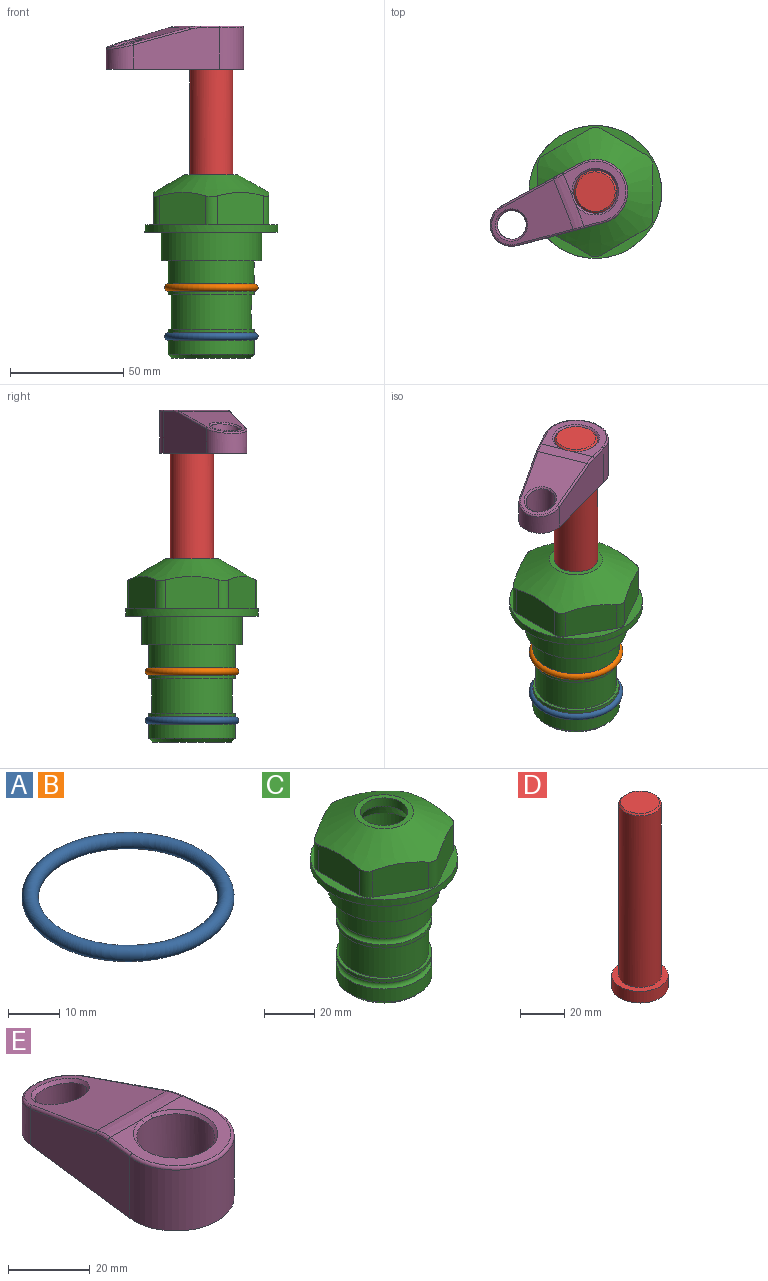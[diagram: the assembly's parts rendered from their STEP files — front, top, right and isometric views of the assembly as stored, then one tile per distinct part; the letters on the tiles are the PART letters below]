
ASSEMBLY  parts=5 mates=4
PART A: 1 faces, bbox 44.7x44.7x3.2 mm
  f0: torus R=19.05mm, axis (0,0,1), area 1193.9mm2
PART B: same geometry as A
PART C: 36 faces, bbox 58.7x58.7x81 mm
  f0: cylinder r=17.78mm len=35.56mm, axis (0,0,1), area 1670.8mm2, adj f23,f24,f31
  f1: cylinder r=19.05mm len=38.1mm, axis (0,0,1), area 1191.9mm2, adj f26,f27,f30
  f2: plane 58.66x58.66mm, normal (0,0,-1), area 1150.6mm2, adj f3,f28
  f3: cylinder r=29.33mm len=58.66mm, axis (0,0,-1), area 585.1mm2, adj f2,f4
  f4: plane 58.66x58.66mm, normal (0,0,1), area 475.9mm2, adj f3,f5,f6,f7,f8,f9,f10,f11
  f5: plane 20.32x14.34mm, normal (-0.5,0.87,0), area 324.4mm2, adj f4,f15,f16,f17
  f6: plane 20.32x14.34mm, normal (0.5,0.87,0), area 324.4mm2, adj f4,f14,f15,f17
  f7: plane 23.48x14.34mm, normal (1,0,0), area 324.4mm2, adj f4,f13,f14,f17
  f8: plane 20.32x14.34mm, normal (0.5,-0.87,0), area 324.4mm2, adj f4,f12,f13,f17
  f9: plane 20.32x14.34mm, normal (-0.5,-0.87,0), area 324.4mm2, adj f4,f11,f12,f17
  f10: plane 23.48x14.34mm, normal (-1,0,0), area 324.4mm2, adj f4,f11,f16,f17
  f11: cylinder r=5.08mm len=12.85mm, axis (0,0,-1), area 67.2mm2, adj f4,f9,f10,f17
  f12: cylinder r=5.08mm len=12.85mm, axis (0,0,-1), area 67.2mm2, adj f4,f8,f9,f17
  f13: cylinder r=5.08mm len=12.85mm, axis (0,0,-1), area 67.2mm2, adj f4,f7,f8,f17
  f14: cylinder r=5.08mm len=12.85mm, axis (0,0,-1), area 67.2mm2, adj f4,f6,f7,f17
  f15: cylinder r=5.08mm len=12.85mm, axis (0,0,-1), area 67.2mm2, adj f4,f5,f6,f17
  f16: cylinder r=5.08mm len=12.85mm, axis (0,0,-1), area 67.2mm2, adj f4,f5,f10,f17
  f17: cone r=11.73mm half-angle=60deg, axis (0,0,-1), area 2071.8mm2, adj f5,f6,f7,f8,f9,f10,f11,f12
  f18: plane 23.46x23.46mm, normal (0,0,1), area 147.4mm2, adj f17,f35
  f19: plane 34.93x34.93mm, normal (0,0,-1), area 958mm2, adj f29
  f20: cylinder r=19.05mm len=38.1mm, axis (0,0,1), area 760.1mm2, adj f21,f29
  f21: torus R=19.05mm, axis (0,0,1), area 565.3mm2, adj f20,f22
  f22: cylinder r=19.05mm len=38.1mm, axis (0,0,1), area 190mm2, adj f21,f23
  f23: plane 38.1x38.1mm, normal (0,0,1), area 146.9mm2, adj f0,f22
  f24: plane 38.1x38.1mm, normal (0,0,-1), area 146.9mm2, adj f0,f25
  f25: cylinder r=19.05mm len=38.1mm, axis (0,0,1), area 190mm2, adj f24,f26
  f26: torus R=19.05mm, axis (0,0,1), area 565.3mm2, adj f1,f25
  f27: plane 44.45x44.45mm, normal (0,0,-1), area 411.7mm2, adj f1,f28
  f28: cylinder r=22.23mm len=44.45mm, axis (0,0,1), area 1773.5mm2, adj f2,f27
  f29: cone r=19.05mm half-angle=45deg, axis (0,0,1), area 257.5mm2, adj f19,f20
  f30: cylinder r=3.17mm len=6.75mm, axis (-1,0,0), area 128mm2, adj f1,f33
  f31: cylinder r=3.17mm len=6.35mm, axis (-1,0,0), area 102.5mm2, adj f0,f33
  f32: plane 25.4x25.4mm, normal (0,0,1), area 506.7mm2, adj f33
  f33: cylinder r=12.7mm len=66.42mm, axis (0,0,-1), area 5236.2mm2, adj f30,f31,f32,f34
  f34: cone r=9.53mm half-angle=30deg, axis (0,0,-1), area 443.4mm2, adj f33,f35
  f35: cylinder r=9.53mm len=19.05mm, axis (0,0,-1), area 240.9mm2, adj f18,f34
PART D: 6 faces, bbox 25.4x25.4x101.6 mm
  f0: plane 17.46x17.46mm, normal (0,0,1), area 239.5mm2, adj f5
  f1: plane 25.4x25.4mm, normal (0,0,-1), area 506.7mm2, adj f2
  f2: cylinder r=12.7mm len=25.4mm, axis (0,0,1), area 506.7mm2, adj f1,f3
  f3: plane 25.4x25.4mm, normal (0,0,1), area 221.7mm2, adj f2,f4
  f4: cylinder r=9.53mm len=94.46mm, axis (0,0,1), area 5653mm2, adj f3,f5
  f5: cone r=8.73mm half-angle=45deg, axis (0,0,-1), area 64.4mm2, adj f0,f4
PART E: 31 faces, bbox 31.7x65.5x19.8 mm
  f0: plane 39.12x18.26mm, normal (0.99,0.12,0), area 612.2mm2, adj f1,f4,f7,f11,f13,f15
  f1: cylinder r=9.53mm len=18.91mm, axis (0,0,-1), area 296.1mm2, adj f0,f2,f7,f17
  f2: plane 39.12x18.26mm, normal (-0.99,0.12,0), area 612.2mm2, adj f1,f4,f7,f12,f14,f16
  f3: cylinder r=6.35mm len=12.7mm, axis (0,0,-1), area 362.4mm2, adj f7,f18
  f4: cylinder r=14.29mm len=28.58mm, axis (0,0,-1), area 882.2mm2, adj f0,f2,f7,f10
  f5: cylinder r=9.53mm len=19.05mm, axis (0,0,-1), area 1092.6mm2, adj f7,f19,f20
  f6: plane 26.99x23.69mm, normal (0,0,1), area 216.2mm2, adj f9,f10,f11,f12,f19
  f7: plane 63.5x28.58mm, normal (0,0,-1), area 661.8mm2, adj f0,f1,f2,f3,f4,f5,f22,f23
  f8: plane 33.52x23.6mm, normal (0,0.26,0.97), area 486mm2, adj f9,f15,f16,f17,f18
  f9: cylinder r=19.05mm len=24.72mm, axis (1,0,0), area 120.4mm2, adj f6,f8,f13,f14,f20
  f10: torus R=13.49mm, axis (0,0,1), area 59mm2, adj f4,f6,f11,f12
  f11: cylinder r=0.79mm len=8.67mm, axis (0.12,-0.99,0), area 10.8mm2, adj f0,f6,f10,f13
  f12: cylinder r=0.79mm len=8.67mm, axis (0.12,0.99,0), area 10.8mm2, adj f2,f6,f10,f14
  f13: bspline ~4.95x1.42mm, area 6.1mm2, adj f0,f9,f11,f15
  f14: bspline ~4.95x1.42mm, area 6.1mm2, adj f2,f9,f12,f16
  f15: cylinder r=0.79mm len=25.95mm, axis (0.12,-0.96,0.26), area 32.9mm2, adj f0,f8,f13,f17
  f16: cylinder r=0.79mm len=25.95mm, axis (0.12,0.96,-0.26), area 32.9mm2, adj f2,f8,f14,f17
  f17: bspline ~18.91x8.38mm, area 30mm2, adj f1,f8,f15,f16
  f18: bspline ~14.29x14.29mm, area 48.3mm2, adj f3,f8
  f19: cone r=9.53mm half-angle=45deg, axis (0,0,1), area 66.5mm2, adj f5,f6,f20
  f20: bspline ~3.22x0.96mm, area 3.5mm2, adj f5,f9,f19
  f21: plane 2.75x2.72mm, normal (0,0,-1), area 2.9mm2, adj f23,f25,f28
  f22: plane 23.05x15.88mm, normal (-0.99,-0.12,0), area 323.6mm2, adj f7,f25,f26,f27,f28,f29
  f23: plane 23.05x15.88mm, normal (0.99,-0.12,0), area 323.6mm2, adj f7,f21,f25,f27,f28,f30
  f24: cylinder r=9.53mm len=10.69mm, axis (0,0,-1), area 114.7mm2, adj f7,f27,f29,f30
  f25: cylinder r=12.7mm len=20.59mm, axis (0,0,-1), area 381.1mm2, adj f7,f21,f22,f23,f26,f28
  f26: plane 2.75x2.72mm, normal (0,0,-1), area 2.9mm2, adj f22,f25,f28
  f27: plane 19.72x18.37mm, normal (0,-0.26,-0.97), area 291.8mm2, adj f22,f23,f24,f28,f29,f30
  f28: cylinder r=15.88mm len=19.92mm, axis (1,0,0), area 54.8mm2, adj f21,f22,f23,f25,f26,f27
  f29: cylinder r=1.59mm len=11mm, axis (0,0,-1), area 34.7mm2, adj f7,f22,f24,f27
  f30: cylinder r=1.59mm len=11mm, axis (0,0,-1), area 34.7mm2, adj f7,f23,f24,f27
PLACE A t=(0,0,-21.59)mm
PLACE B at identity
PLACE C at identity fixed
PLACE D rot(axis=(0,0,1),111.7deg) t=(0,0,27.55)mm
PLACE E rot(axis=(0,0,1),111.7deg) t=(0,0,27.55)mm
MATE fastened A.f0 <-> C.f0  axis (0,0,1) through (0,0,-46.1)mm
MATE fastened B.f0 <-> C.f0  axis (0,0,1) through (0,0,-24.51)mm
MATE fastened D.f2 <-> E.f4  axis (0,0,1) through (0,0,91.05)mm
MATE cylindrical C.f0 <-> D.f2  axis (0,0,1) through (0,0,-50.55)mm
